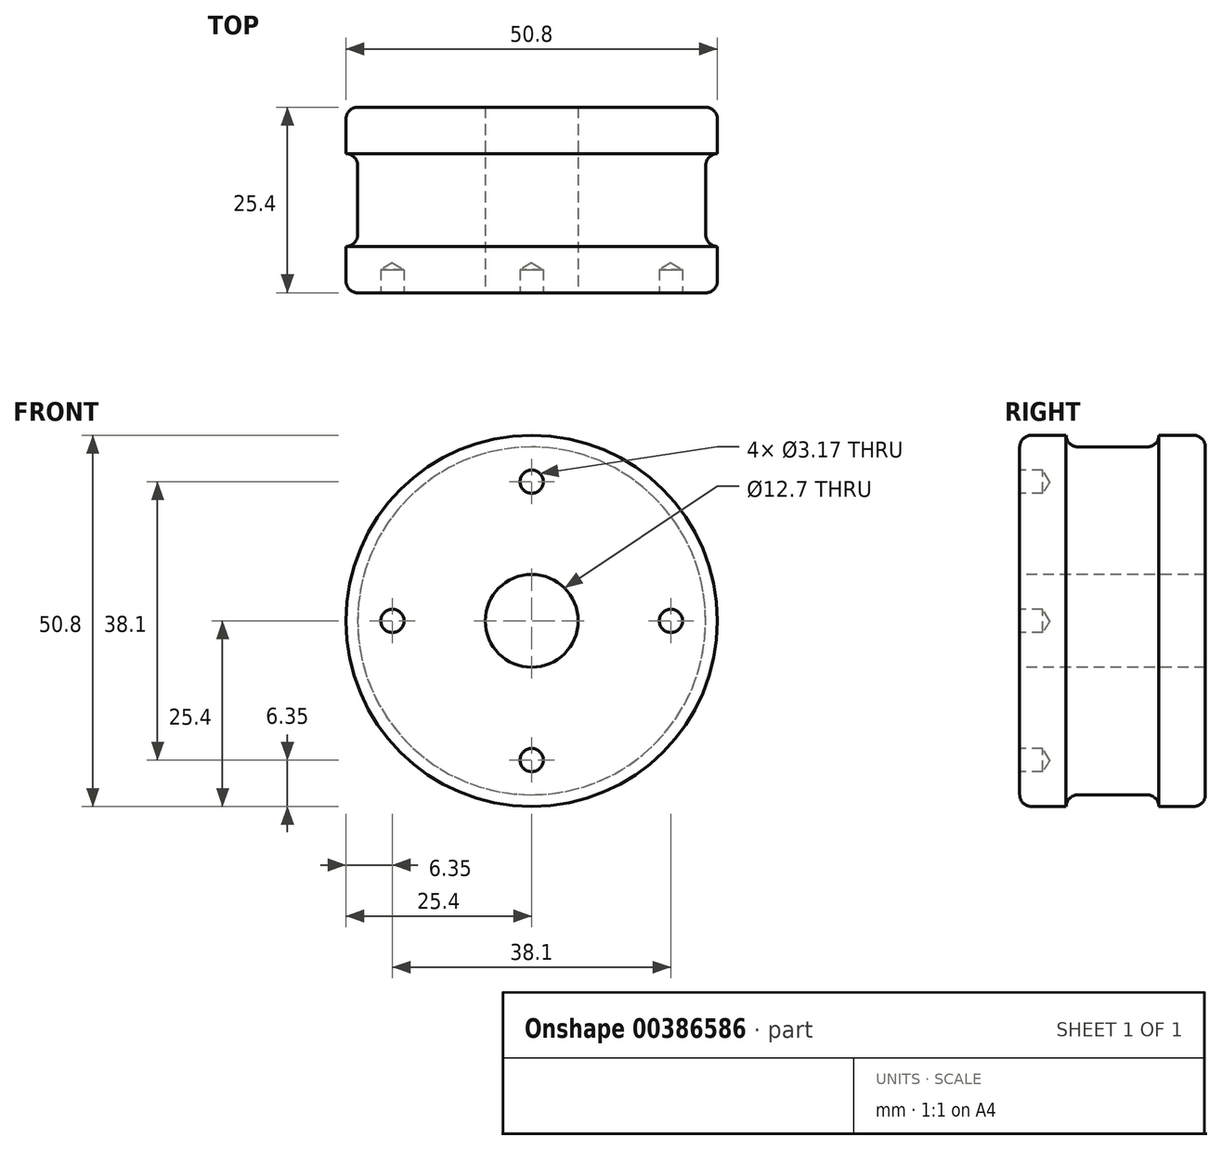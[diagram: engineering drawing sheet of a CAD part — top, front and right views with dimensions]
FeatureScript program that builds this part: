
annotation { "Feature Type Name" : "Feature", "Feature Type Description" : "" }
export const myFeature = defineFeature(function(context is Context, id is Id, definition is map)
    precondition{}
    {
        {
            var Q0;
            Q0=qCreatedBy(makeId("Front.planeOp"),FACE);
            var sketch = newSketch(context, id + "F0", { "sketchPlane" : qUnion([Q0])});
            skCircle(sketch, "E0", {"center": v(0, 0) * mm, "radius": 25.4 * mm});
            skSolve(sketch);
        }
        {
            var Q0;
            Q0 = qSketchRegion(id + "F0", true);
            extrude(context, id + "F1", {"entities" : qUnion([Q0]), "depth" : 6.35 * mm});
        }
        {
            var Q0;
            Q0=makeQuery(id+"F1.opExtrude","CAP_FACE",FACE,{"disambiguationData":[OSD([sQuery(id+"F0.wireOp",EDGE,"E0")])],"isStart":false});
            var sketch = newSketch(context, id + "F2", { "sketchPlane" : qUnion([Q0])});
            skCircle(sketch, "E1", {"center": v(0, 0) * mm, "radius": 23.81 * mm});
            skSolve(sketch);
        }
        {
            var Q0;
            Q0 = qSketchRegion(id + "F2", true);
            extrude(context, id + "F3", {"entities" : qUnion([Q0]), "operationType" : NewBodyOperationType.ADD, "depth" : 12.7 * mm});
        }
        {
            var Q0;
            Q0=makeQuery(id+"F3.opExtrude","CAP_FACE",FACE,{"disambiguationData":[OSD([sQuery(id+"F2.wireOp",EDGE,"E1")])],"isStart":false});
            var sketch = newSketch(context, id + "F4", { "sketchPlane" : qUnion([Q0])});
            skCircle(sketch, "E2", {"center": v(0, 0) * mm, "radius": 25.4 * mm});
            skSolve(sketch);
        }
        {
            var Q0;
            Q0 = qSketchRegion(id + "F4", true);
            extrude(context, id + "F5", {"entities" : qUnion([Q0]), "operationType" : NewBodyOperationType.ADD, "depth" : 6.35 * mm});
        }
        {
            var Q0;
            Q0=makeQuery(id+"F5.opExtrude","CAP_FACE",FACE,{"disambiguationData":[OSD([sQuery(id+"F4.wireOp",EDGE,"E2")])],"isStart":false});
            var sketch = newSketch(context, id + "F6", { "sketchPlane" : qUnion([Q0])});
            skCircle(sketch, "E3", {"center": v(0, 0) * mm, "radius": 6.35 * mm});
            skSolve(sketch);
        }
        {
            var Q0;
            Q0 = qSketchRegion(id + "F6", true);
            extrude(context, id + "F7", {"entities" : qUnion([Q0]), "operationType" : NewBodyOperationType.REMOVE, "endBound" : BoundingType.THROUGH_ALL, "oppositeDirection" : true, "depth" : 25.4 * mm});
        }
        {
            var Q0;
            Q0=makeQuery(id+"F5.opExtrude","CAP_FACE",FACE,{"disambiguationData":[OSD([sQuery(id+"F4.wireOp",EDGE,"E2")])],"isStart":false});
            var sketch = newSketch(context, id + "F8", { "sketchPlane" : qUnion([Q0])});
            skPoint(sketch, "E4", {"position": v(0, 19.05) * mm});
            skPoint(sketch, "E5", {"position": v(19.05, 0) * mm});
            skPoint(sketch, "E6", {"position": v(0, -19.05) * mm});
            skPoint(sketch, "E7", {"position": v(-19.05, 0) * mm});
            skSolve(sketch);
        }
        {
            var Q0;
            Q0=sQuery(id+"F8.wireOp",VERTEX,"E4");
            var Q1;
            Q1=sQuery(id+"F8.wireOp",VERTEX,"E6");
            var Q2;
            Q2=sQuery(id+"F8.wireOp",VERTEX,"E7");
            var Q3;
            Q3=sQuery(id+"F8.wireOp",VERTEX,"E5");
            var Q4;
            Q4=makeQuery(id+"F1.opExtrude","SWEPT_BODY",BODY,{"disambiguationData":[OSD([sQuery(id+"F0.wireOp",EDGE,"E0")])]});
            hole(context, id + "F9", {"style" : HoleStyle.SIMPLE, "endStyle" : HoleEndStyle.BLIND, "holeDiameter" : 3.17 * mm, "holeDepth" : 3.17 * mm, "isTappedThrough" : true, "tappedDepth" : 12.7 * mm, "tapClearance" : 3, "locations" : qUnion([Q0, Q1, Q2, Q3]), "scope" : qUnion([Q4])});
        }
        {
            var Q0;
            Q0=makeQuery(id+"F3.opExtrude","SWEPT_FACE",FACE,{"disambiguationData":[OSD([sQuery(id+"F2.wireOp",EDGE,"E1")])]});
            var Q1;
            Q1=makeQuery(id+"F5.opExtrude","CAP_EDGE",EDGE,{"disambiguationData":[OSD([sQuery(id+"F4.wireOp",EDGE,"E2")])],"isStart":false});
            var Q2;
            Q2=makeQuery(id+"F1.opExtrude","CAP_EDGE",EDGE,{"disambiguationData":[OSD([sQuery(id+"F0.wireOp",EDGE,"E0")])],"isStart":true});
            fillet(context, id + "F10", {"entities" : qUnion([Q0, Q1, Q2]), "radius" : 1.6 * mm, "tangentPropagation" : true, "allowEdgeOverflow" : false});
        }
    });
